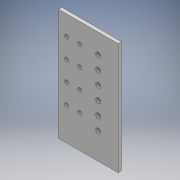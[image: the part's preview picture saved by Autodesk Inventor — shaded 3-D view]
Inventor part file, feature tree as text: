
AUTODESK INVENTOR PART (.ipt)
format: ipt  version: 2018 (Build 220112000, 112)  size: 129,536 bytes
history: native  units: mm
features: extrude x4, sketch x4, pattern_linear x2
ambient origin geometry x8: Origin, YZ Plane, XZ Plane, XY Plane, X Axis, Y Axis, Z Axis, Center Point
bodies: Solid1 (feature_tree)
feature tree (10):
  extrude  "Extrusion1"  Depth=170.0mm
  extrude  "Extrusion2"  Depth=5.0mm
  pattern_linear  "Rectangular Pattern1"  Count1=6  [1 undecoded]
  extrude  "Extrusion3"  Depth=5.0mm TaperAngle=0.0deg
  pattern_linear  "Rectangular Pattern2"  Count1=2  [1 undecoded]
  extrude  "Extrusion4"  Depth=5.0mm
  sketch  "Sketch1"  dims[d0=150.0mm d1=170.0mm]
  sketch  "Sketch2"  dims[d2=5.0mm d3=0.0mm d4=7.5mm]
  sketch  "Sketch3"  dims[d5=5.0mm d6=0.0mm d7=60.0mm d9=20.0mm]
  sketch  "Sketch4"  dims[d10=6.0mm d11=5.0mm d12=0.0mm d13=20.0mm d15=20.0mm d16=40.0mm d18=30.0mm d19=59.75mm d20=0.0mm]
note: 2 required parameter values undecoded (feature->parameter linkage not recoverable at this tier; creation-order binding heuristic only, values carry confidence <= 0.55)
